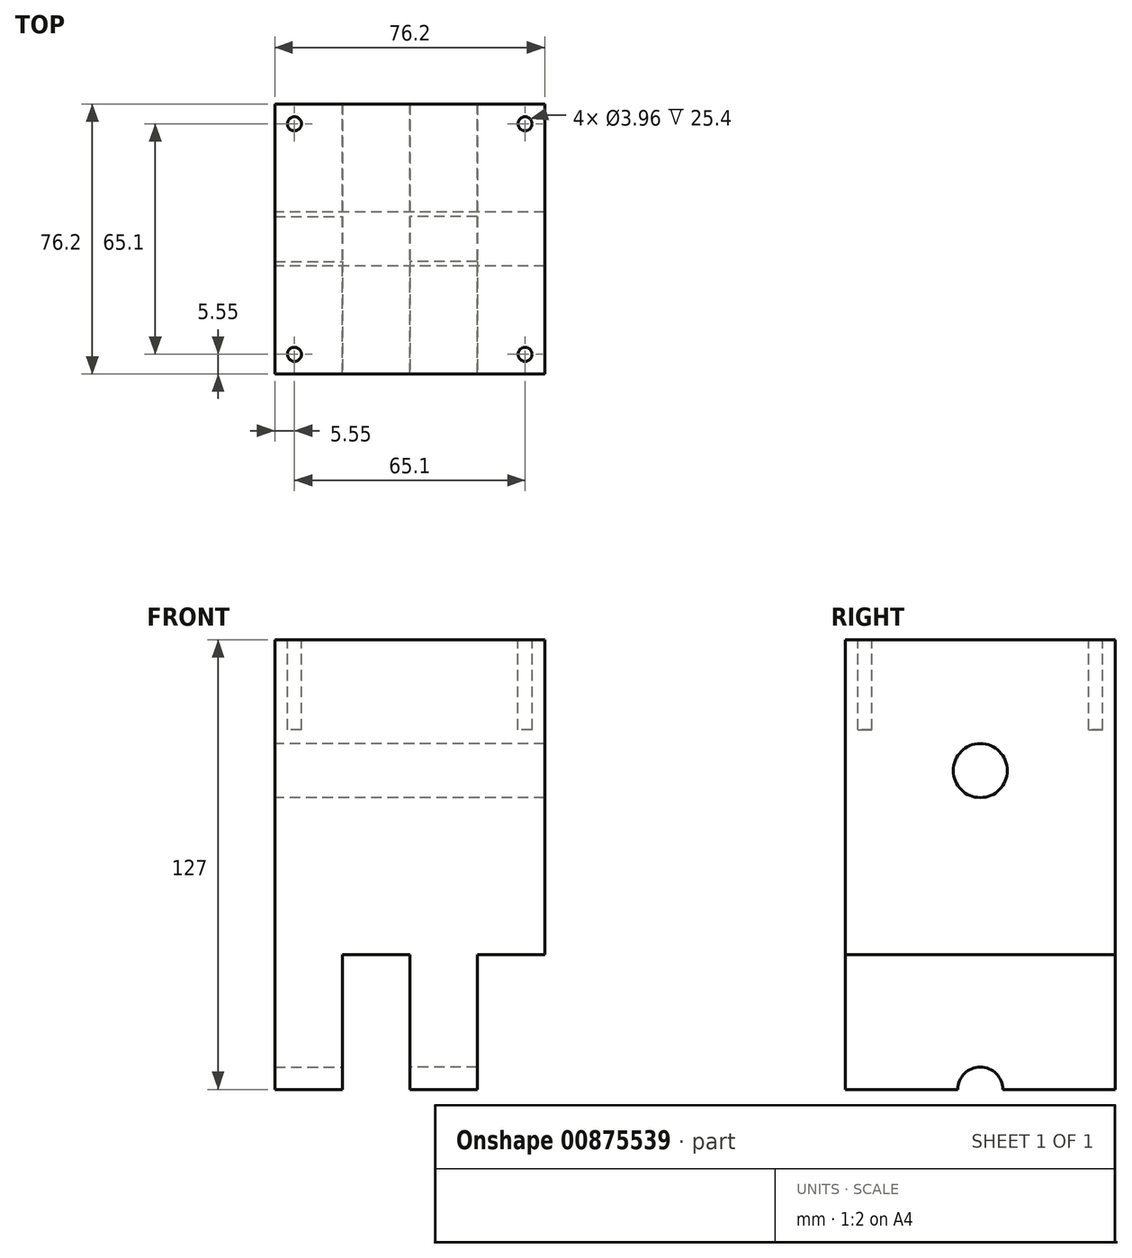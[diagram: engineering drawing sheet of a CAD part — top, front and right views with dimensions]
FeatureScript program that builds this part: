
annotation { "Feature Type Name" : "Feature", "Feature Type Description" : "" }
export const myFeature = defineFeature(function(context is Context, id is Id, definition is map)
    precondition{}
    {
        {
            var Q0;
            Q0=qCreatedBy(makeId("Right.planeOp"),FACE);
            var sketch = newSketch(context, id + "F0", { "sketchPlane" : qUnion([Q0])});
            skLineSegment(sketch, "E0.bottom", {"start": v(38.1, -63.5) * mm, "end": v(-38.1, -63.5) * mm});
            skLineSegment(sketch, "E0.top", {"start": v(38.1, 63.5) * mm, "end": v(-38.1, 63.5) * mm});
            skLineSegment(sketch, "E0.left", {"start": v(38.1, -63.5) * mm, "end": v(38.1, 63.5) * mm});
            skLineSegment(sketch, "E0.right", {"start": v(-38.1, -63.5) * mm, "end": v(-38.1, 63.5) * mm});
            skPoint(sketch, "E0.middle", {"position": v(0, 0) * mm});
            skArc(sketch, "E1", {"start": v(38.1, -63.5) * mm, "mid": v(0, -101.6) * mm, "end": v(-38.1, -63.5) * mm});
            skCircle(sketch, "E2", {"center": v(0, -63.5) * mm, "radius": 6.35 * mm});
            skLineSegment(sketch, "E3", {"start": v(-38.1, -25.4) * mm, "end": v(38.1, -25.4) * mm});
            skCircle(sketch, "E4", {"center": v(0, 26.52) * mm, "radius": 7.62 * mm});
            skSolve(sketch);
        }
        {
            var Q0;
            {var subQ0=sQuery(id+"F0.wireOp",EDGE,"E0.top");Q0=makeQuery(id+"F0.imprint","IMPRINT",FACE,{"disambiguationData":[TD([[makeQuery(id+"F0.imprint","IMPRINT",EDGE,{"derivedFrom":subQ0}),1.0]])]});}
            extrude(context, id + "F1", {"entities" : qUnion([Q0]), "endBound" : BoundingType.SYMMETRIC, "depth" : 76.2 * mm, "offsetDistance" : 25.4 * mm});
        }
        {
            var Q0;
            {var subQ4=sQuery(id+"F0.wireOp",EDGE,"E3");Q0=makeQuery(id+"F0.imprint","IMPRINT",FACE,{"disambiguationData":[TD([[makeQuery(id+"F0.imprint","IMPRINT",EDGE,{"derivedFrom":subQ4}),-1.0]])]});}
            var Q1;
            {var subQ0=sQuery(id+"F0.wireOp",EDGE,"E1");Q1=makeQuery(id+"F0.imprint","IMPRINT",FACE,{"disambiguationData":[TD([[makeQuery(id+"F0.imprint","IMPRINT",EDGE,{"derivedFrom":subQ0}),-1.0]])]});}
            extrude(context, id + "F2", {"entities" : qUnion([Q0, Q1]), "operationType" : NewBodyOperationType.ADD, "depth" : 19.05 * mm, "offsetDistance" : 25.4 * mm});
        }
        {
            var Q0;
            {var subQ4=sQuery(id+"F0.wireOp",EDGE,"E3");Q0=makeQuery(id+"F0.imprint","IMPRINT",FACE,{"disambiguationData":[TD([[makeQuery(id+"F0.imprint","IMPRINT",EDGE,{"derivedFrom":subQ4}),-1.0]])]});}
            var Q1;
            {var subQ0=sQuery(id+"F0.wireOp",EDGE,"E1");Q1=makeQuery(id+"F0.imprint","IMPRINT",FACE,{"disambiguationData":[TD([[makeQuery(id+"F0.imprint","IMPRINT",EDGE,{"derivedFrom":subQ0}),-1.0]])]});}
            extrude(context, id + "F3", {"entities" : qUnion([Q0, Q1]), "operationType" : NewBodyOperationType.ADD, "oppositeDirection" : true, "depth" : 38.1 * mm, "offsetDistance" : 25.4 * mm, "hasSecondDirection" : true, "secondDirectionOppositeDirection" : true, "secondDirectionDepth" : 19.05 * mm});
        }
        {
            var Q0;
            Q0=makeQuery(id+"F1.opExtrude","SWEPT_FACE",FACE,{"disambiguationData":[OSD([sQuery(id+"F0.wireOp",EDGE,"E0.top")])]});
            var sketch = newSketch(context, id + "F4", { "sketchPlane" : qUnion([Q0])});
            skLineSegment(sketch, "E5.bottom", {"start": v(32.55, -32.55) * mm, "end": v(-32.55, -32.55) * mm});
            skLineSegment(sketch, "E5.top", {"start": v(32.55, 32.55) * mm, "end": v(-32.55, 32.55) * mm});
            skLineSegment(sketch, "E5.left", {"start": v(32.55, -32.55) * mm, "end": v(32.55, 32.55) * mm});
            skLineSegment(sketch, "E5.right", {"start": v(-32.55, -32.55) * mm, "end": v(-32.55, 32.55) * mm});
            skPoint(sketch, "E5.middle", {"position": v(0, 0) * mm});
            skCircle(sketch, "E6", {"center": v(-32.55, 32.55) * mm, "radius": 1.98 * mm});
            skCircle(sketch, "E7", {"center": v(32.55, 32.55) * mm, "radius": 1.98 * mm});
            skCircle(sketch, "E8", {"center": v(32.55, -32.55) * mm, "radius": 1.98 * mm});
            skCircle(sketch, "E9", {"center": v(-32.55, -32.55) * mm, "radius": 1.98 * mm});
            skSolve(sketch);
        }
        {
            var Q0;
            {var subQ0=sQuery(id+"F4.wireOp",EDGE,"E5.right");var subQ1=sQuery(id+"F4.wireOp",EDGE,"E5.top");var subQ2=makeQuery(id+"F4.imprint","INTERSECT",VERTEX,{"derivedFrom":[subQ1,subQ0]});Q0=makeQuery(id+"F4.imprint","IMPRINT",FACE,{"disambiguationData":[TD([[makeQuery(id+"F4.imprint","IMPRINT",EDGE,{"disambiguationData":[TD([[subQ2,1.0]])],"derivedFrom":subQ1}),-1.0]])]});}
            var Q1;
            {var subQ0=sQuery(id+"F4.wireOp",EDGE,"E5.right");var subQ1=sQuery(id+"F4.wireOp",EDGE,"E5.top");var subQ2=makeQuery(id+"F4.imprint","INTERSECT",VERTEX,{"derivedFrom":[subQ1,subQ0]});Q1=makeQuery(id+"F4.imprint","IMPRINT",FACE,{"disambiguationData":[TD([[makeQuery(id+"F4.imprint","IMPRINT",EDGE,{"disambiguationData":[TD([[subQ2,1.0]])],"derivedFrom":subQ1}),1.0]])]});}
            var Q2;
            {var subQ0=sQuery(id+"F4.wireOp",EDGE,"E5.left");var subQ1=sQuery(id+"F4.wireOp",EDGE,"E5.top");var subQ2=makeQuery(id+"F4.imprint","INTERSECT",VERTEX,{"derivedFrom":[subQ1,subQ0]});Q2=makeQuery(id+"F4.imprint","IMPRINT",FACE,{"disambiguationData":[TD([[makeQuery(id+"F4.imprint","IMPRINT",EDGE,{"disambiguationData":[TD([[subQ2,-1.0]])],"derivedFrom":subQ1}),1.0]])]});}
            var Q3;
            {var subQ0=sQuery(id+"F4.wireOp",EDGE,"E5.left");var subQ1=sQuery(id+"F4.wireOp",EDGE,"E5.top");var subQ2=makeQuery(id+"F4.imprint","INTERSECT",VERTEX,{"derivedFrom":[subQ1,subQ0]});Q3=makeQuery(id+"F4.imprint","IMPRINT",FACE,{"disambiguationData":[TD([[makeQuery(id+"F4.imprint","IMPRINT",EDGE,{"disambiguationData":[TD([[subQ2,-1.0]])],"derivedFrom":subQ1}),-1.0]])]});}
            var Q4;
            {var subQ0=sQuery(id+"F4.wireOp",EDGE,"E5.right");var subQ1=sQuery(id+"F4.wireOp",EDGE,"E5.bottom");var subQ2=makeQuery(id+"F4.imprint","INTERSECT",VERTEX,{"derivedFrom":[subQ1,subQ0]});Q4=makeQuery(id+"F4.imprint","IMPRINT",FACE,{"disambiguationData":[TD([[makeQuery(id+"F4.imprint","IMPRINT",EDGE,{"disambiguationData":[TD([[subQ2,1.0]])],"derivedFrom":subQ1}),1.0]])]});}
            var Q5;
            {var subQ0=sQuery(id+"F4.wireOp",EDGE,"E5.right");var subQ1=sQuery(id+"F4.wireOp",EDGE,"E5.bottom");var subQ2=makeQuery(id+"F4.imprint","INTERSECT",VERTEX,{"derivedFrom":[subQ1,subQ0]});Q5=makeQuery(id+"F4.imprint","IMPRINT",FACE,{"disambiguationData":[TD([[makeQuery(id+"F4.imprint","IMPRINT",EDGE,{"disambiguationData":[TD([[subQ2,1.0]])],"derivedFrom":subQ1}),-1.0]])]});}
            var Q6;
            {var subQ0=sQuery(id+"F4.wireOp",EDGE,"E5.left");var subQ1=sQuery(id+"F4.wireOp",EDGE,"E5.bottom");var subQ2=makeQuery(id+"F4.imprint","INTERSECT",VERTEX,{"derivedFrom":[subQ1,subQ0]});Q6=makeQuery(id+"F4.imprint","IMPRINT",FACE,{"disambiguationData":[TD([[makeQuery(id+"F4.imprint","IMPRINT",EDGE,{"disambiguationData":[TD([[subQ2,-1.0]])],"derivedFrom":subQ1}),1.0]])]});}
            var Q7;
            {var subQ0=sQuery(id+"F4.wireOp",EDGE,"E5.left");var subQ1=sQuery(id+"F4.wireOp",EDGE,"E5.bottom");var subQ2=makeQuery(id+"F4.imprint","INTERSECT",VERTEX,{"derivedFrom":[subQ1,subQ0]});Q7=makeQuery(id+"F4.imprint","IMPRINT",FACE,{"disambiguationData":[TD([[makeQuery(id+"F4.imprint","IMPRINT",EDGE,{"disambiguationData":[TD([[subQ2,-1.0]])],"derivedFrom":subQ1}),-1.0]])]});}
            extrude(context, id + "F5", {"entities" : qUnion([Q0, Q1, Q2, Q3, Q4, Q5, Q6, Q7]), "operationType" : NewBodyOperationType.REMOVE, "oppositeDirection" : true, "depth" : 25.4 * mm, "offsetDistance" : 25.4 * mm});
        }
    });
